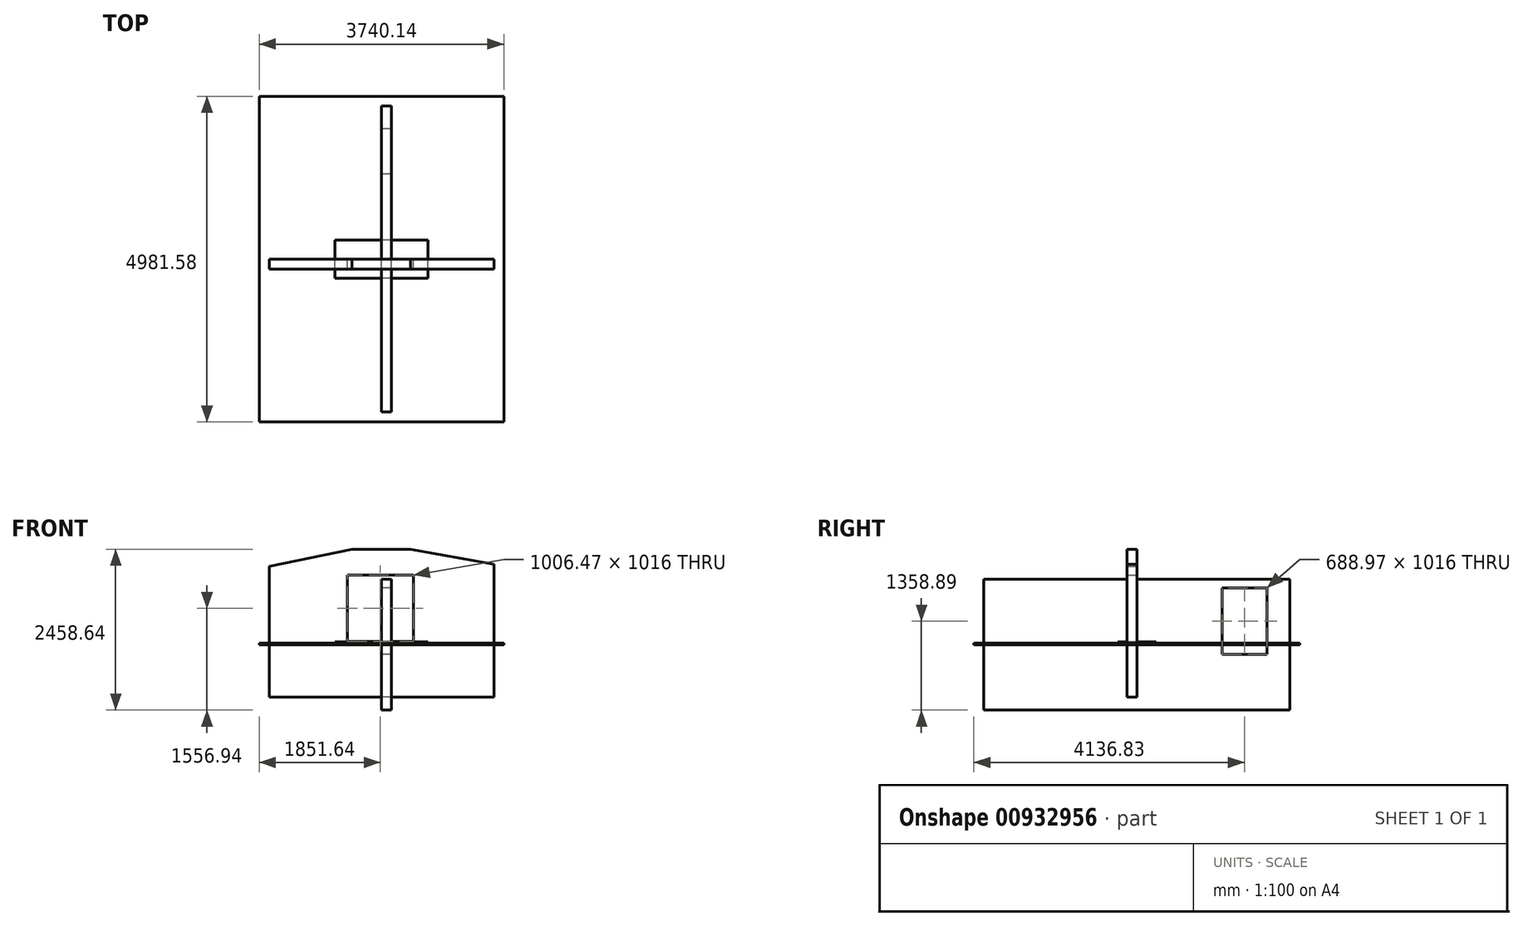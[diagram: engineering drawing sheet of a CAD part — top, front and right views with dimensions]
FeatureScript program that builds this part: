
annotation { "Feature Type Name" : "Feature", "Feature Type Description" : "" }
export const myFeature = defineFeature(function(context is Context, id is Id, definition is map)
    precondition{}
    {
        {
            var Q0;
            Q0=qCreatedBy(makeId("Top.planeOp"),FACE);
            var sketch = newSketch(context, id + "F0", { "sketchPlane" : qUnion([Q0])});
            skLineSegment(sketch, "E0.bottom", {"start": v(1870.07, 2490.79) * mm, "end": v(-1870.08, 2490.79) * mm});
            skLineSegment(sketch, "E0.top", {"start": v(1870.08, -2490.79) * mm, "end": v(-1870.07, -2490.79) * mm});
            skLineSegment(sketch, "E0.left", {"start": v(1870.07, 2490.79) * mm, "end": v(1870.08, -2490.79) * mm});
            skLineSegment(sketch, "E0.right", {"start": v(-1870.08, 2490.79) * mm, "end": v(-1870.07, -2490.79) * mm});
            skPoint(sketch, "E0.middle", {"position": v(0, 0) * mm});
            skSolve(sketch);
        }
        {
            var Q0;
            Q0 = qSketchRegion(id + "F0", true);
            extrude(context, id + "F1", {"entities" : qUnion([Q0]), "depth" : 25.4 * mm, "offsetDistance" : 25.4 * mm});
        }
        {
            var Q0;
            Q0=qCreatedBy(makeId("Right.planeOp"),FACE);
            var sketch = newSketch(context, id + "F2", { "sketchPlane" : qUnion([Q0])});
            skLineSegment(sketch, "E1.bottom", {"start": v(2339.98, -1000.13) * mm, "end": v(-2339.98, -1000.13) * mm});
            skLineSegment(sketch, "E1.top", {"start": v(2339.97, 1000.13) * mm, "end": v(-2339.98, 1000.12) * mm});
            skLineSegment(sketch, "E1.left", {"start": v(2339.98, -1000.13) * mm, "end": v(2339.98, 1000.13) * mm});
            skLineSegment(sketch, "E1.right", {"start": v(-2339.97, -1000.13) * mm, "end": v(-2339.98, 1000.12) * mm});
            skPoint(sketch, "E1.middle", {"position": v(0, 0) * mm});
            skLineSegment(sketch, "E2.bottom", {"start": v(1990.53, -149.23) * mm, "end": v(1301.56, -149.23) * mm});
            skLineSegment(sketch, "E2.top", {"start": v(1990.53, 866.77) * mm, "end": v(1301.56, 866.77) * mm});
            skLineSegment(sketch, "E2.left", {"start": v(1990.53, -149.22) * mm, "end": v(1990.53, 866.77) * mm});
            skLineSegment(sketch, "E2.right", {"start": v(1301.56, -149.23) * mm, "end": v(1301.56, 866.77) * mm});
            skSolve(sketch);
        }
        {
            var Q0;
            Q0=makeQuery(id+"F2.imprint","IMPRINT",FACE,{"disambiguationData":[TD([[makeQuery(id+"F2.imprint","IMPRINT",EDGE,{"derivedFrom":sQuery(id+"F2.wireOp",EDGE,"E1.bottom")}),-1.0]])]});
            var Q1;
            Q1 = qSketchRegion(id + "FQkdplFcYzkr4WS_2", true);
            extrude(context, id + "F3", {"entities" : qUnion([Q0, Q1]), "depth" : 152.4 * mm, "offsetDistance" : 25.4 * mm});
        }
        {
            var Q0;
            Q0=qCreatedBy(makeId("Front.planeOp"),FACE);
            var sketch = newSketch(context, id + "F4", { "sketchPlane" : qUnion([Q0])});
            skLineSegment(sketch, "E3", {"start": v(1716.71, -802.08) * mm, "end": v(-1718.64, -802.08) * mm});
            skLineSegment(sketch, "E4", {"start": v(-1718.64, -802.08) * mm, "end": v(-1718.64, 1198.17) * mm});
            skLineSegment(sketch, "E5", {"start": v(-1718.64, 1198.17) * mm, "end": v(-449.67, 1458.52) * mm});
            skLineSegment(sketch, "E6", {"start": v(-449.67, 1458.52) * mm, "end": v(441.96, 1458.52) * mm});
            skLineSegment(sketch, "E7", {"start": v(441.96, 1458.52) * mm, "end": v(1716.71, 1228.16) * mm});
            skLineSegment(sketch, "E8", {"start": v(1716.71, 1228.16) * mm, "end": v(1716.71, -802.08) * mm});
            skSolve(sketch);
        }
        {
            var Q0;
            Q0 = qSketchRegion(id + "F4", true);
            extrude(context, id + "F5", {"entities" : qUnion([Q0]), "depth" : 152.4 * mm, "offsetDistance" : 25.4 * mm});
        }
        {
            var Q0;
            Q0=makeQuery(id+"F5.opExtrude","CAP_FACE",FACE,{"disambiguationData":[OSD([sQuery(id+"F4.wireOp",EDGE,"E3"),sQuery(id+"F4.wireOp",EDGE,"E4"),sQuery(id+"F4.wireOp",EDGE,"E5"),sQuery(id+"F4.wireOp",EDGE,"E6"),sQuery(id+"F4.wireOp",EDGE,"E7"),sQuery(id+"F4.wireOp",EDGE,"E8")])],"isStart":true});
            var sketch = newSketch(context, id + "F6", { "sketchPlane" : qUnion([Q0])});
            skLineSegment(sketch, "E9.bottom", {"start": v(-484.81, 48.82) * mm, "end": v(521.66, 48.82) * mm});
            skLineSegment(sketch, "E9.top", {"start": v(-484.81, 1064.82) * mm, "end": v(521.66, 1064.82) * mm});
            skLineSegment(sketch, "E9.left", {"start": v(-484.81, 48.82) * mm, "end": v(-484.81, 1064.82) * mm});
            skLineSegment(sketch, "E9.right", {"start": v(521.66, 48.82) * mm, "end": v(521.66, 1064.82) * mm});
            skSolve(sketch);
        }
        {
            var Q0;
            Q0 = qSketchRegion(id + "F6", true);
            extrude(context, id + "F7", {"entities" : qUnion([Q0]), "operationType" : NewBodyOperationType.REMOVE, "oppositeDirection" : true, "depth" : 152.4 * mm, "offsetDistance" : 25.4 * mm});
        }
        {
            var Q0;
            Q0=qCreatedBy(makeId("Top.planeOp"),FACE);
            var sketch = newSketch(context, id + "F8", { "sketchPlane" : qUnion([Q0])});
            skLineSegment(sketch, "E10.bottom", {"start": v(711.2, -292.1) * mm, "end": v(-711.2, -292.1) * mm});
            skLineSegment(sketch, "E10.top", {"start": v(711.2, 292.1) * mm, "end": v(-711.2, 292.1) * mm});
            skLineSegment(sketch, "E10.left", {"start": v(711.2, -292.1) * mm, "end": v(711.2, 292.1) * mm});
            skLineSegment(sketch, "E10.right", {"start": v(-711.2, -292.1) * mm, "end": v(-711.2, 292.1) * mm});
            skPoint(sketch, "E10.middle", {"position": v(0, 0) * mm});
            skSolve(sketch);
        }
        {
            var Q0;
            Q0 = qSketchRegion(id + "F8", true);
            extrude(context, id + "F9", {"entities" : qUnion([Q0]), "depth" : 44.45 * mm, "offsetDistance" : 25.4 * mm});
        }
    });
